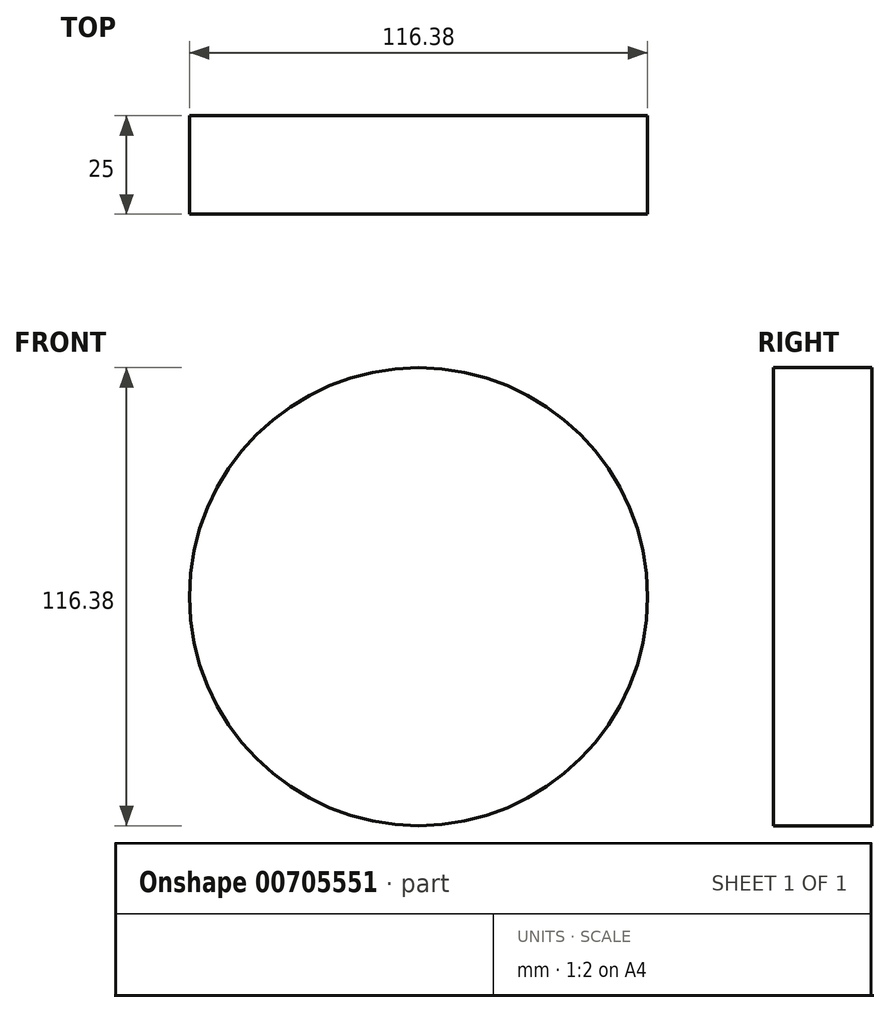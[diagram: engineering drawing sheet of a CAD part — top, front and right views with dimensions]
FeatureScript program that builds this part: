
annotation { "Feature Type Name" : "Feature", "Feature Type Description" : "" }
export const myFeature = defineFeature(function(context is Context, id is Id, definition is map)
    precondition{}
    {
        {
            var Q0;
            Q0=qCreatedBy(makeId("Front.planeOp"),FACE);
            var sketch = newSketch(context, id + "F0", { "sketchPlane" : qUnion([Q0])});
            skCircle(sketch, "E0", {"center": v(0, 0) * mm, "radius": 58.19 * mm});
            skSolve(sketch);
        }
        {
            var Q0;
            Q0=sQuery(id+"F0.wireOp",EDGE,"E0");
            extrude(context, id + "F1", {"bodyType" : ToolBodyType.SURFACE, "surfaceEntities" : qUnion([Q0]), "depth" : 25 * mm, "offsetDistance" : 25 * mm});
        }
    });
